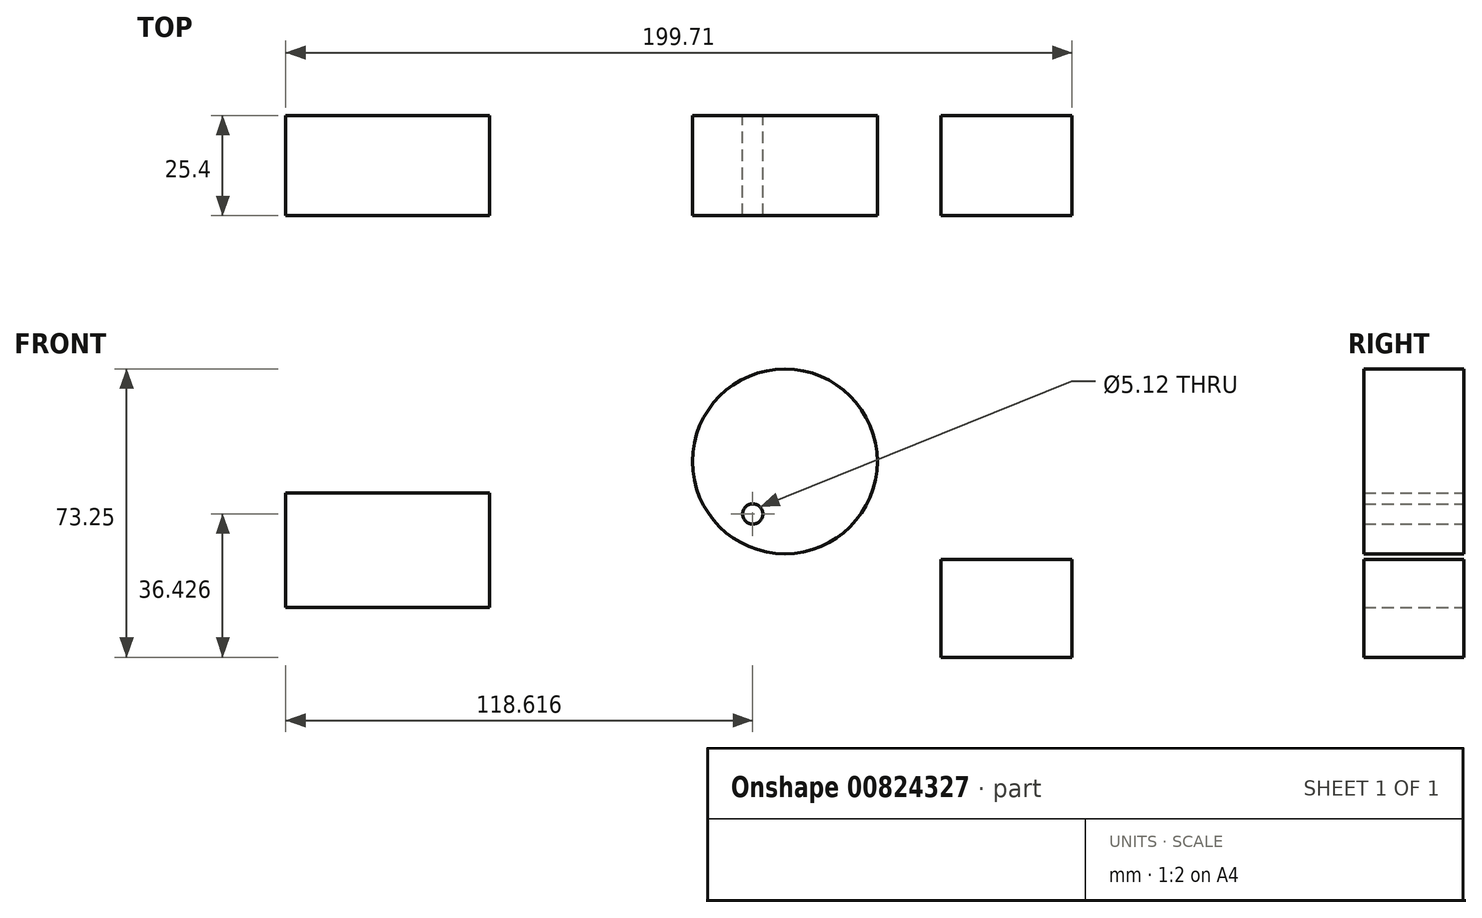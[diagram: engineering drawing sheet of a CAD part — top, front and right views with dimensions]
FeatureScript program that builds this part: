
annotation { "Feature Type Name" : "Feature", "Feature Type Description" : "" }
export const myFeature = defineFeature(function(context is Context, id is Id, definition is map)
    precondition{}
    {
        {
            var Q0;
            Q0=qCreatedBy(makeId("Front.planeOp"),FACE);
            var sketch = newSketch(context, id + "F0", { "sketchPlane" : qUnion([Q0])});
            skLineSegment(sketch, "E0.bottom", {"start": v(-111.19, 57.96) * mm, "end": v(-59.46, 57.96) * mm});
            skLineSegment(sketch, "E0.top", {"start": v(-111.19, 28.86) * mm, "end": v(-59.46, 28.86) * mm});
            skLineSegment(sketch, "E0.left", {"start": v(-111.19, 57.96) * mm, "end": v(-111.19, 28.86) * mm});
            skLineSegment(sketch, "E0.right", {"start": v(-59.46, 57.96) * mm, "end": v(-59.46, 28.86) * mm});
            skCircle(sketch, "E1", {"center": v(15.6, 66) * mm, "radius": 23.48 * mm});
            skCircle(sketch, "E2", {"center": v(7.43, 52.66) * mm, "radius": 2.56 * mm});
            skLineSegment(sketch, "E3.bottom", {"start": v(55.26, 41.08) * mm, "end": v(88.52, 41.08) * mm});
            skLineSegment(sketch, "E3.top", {"start": v(55.26, 16.23) * mm, "end": v(88.52, 16.23) * mm});
            skLineSegment(sketch, "E3.left", {"start": v(55.26, 41.08) * mm, "end": v(55.26, 16.23) * mm});
            skLineSegment(sketch, "E3.right", {"start": v(88.52, 41.08) * mm, "end": v(88.52, 16.23) * mm});
            skSolve(sketch);
        }
        {
            var Q0;
            Q0 = qSketchRegion(id + "F0", true);
            extrude(context, id + "F1", {"entities" : qUnion([Q0]), "depth" : 25.4 * mm, "offsetDistance" : 25.4 * mm});
        }
    });
